# Revit family: P191568KX-114c_KSDG950E
name_source: partatom
category: Specialty Equipment
units: mm (PartAtom-declared; Revit-internal decimal feet)

## family parameters
Always vertical = Yes
Cut with Voids When Loaded = No
Enable Cutting in Views = No
Maintain Annotation Orientation = No
Part Type = Normal
Room Calculation Point = No
Round Connector Dimension = Use Diameter
Shared = No
Work Plane-Based = No

## types (1)
- KSDG950ESS
    Apparent Load = 40 VA
    Body Material = ARCAT - Metal - Steel - Stainless
    Clearance Material = ARCAT - Clearance
    Cooking Grate Material = ARCAT - Metal - Cast Iron 1/4" Plate
    Default Elevation = 0"
    Depth = 28 7/8"
    Description = 30-Inch 4-Burner Dual Fuel Downdraft Slide-In Range
Cuisinière bi-combustible à commandes frontales, 4 brûleurs, 30 po
    Dimension Guide = http://access.whirlpool.com Guide&sku=KSDG950ESS&language=EN
http://access.whirlpool.com Guide&sku=KSDG950ESS&language=FR
    Door Material = ARCAT - Metal - Steel - Stainless
    Family Name = COOKING
    Feature 1 = Downdraft
Évacuation descendante
    Feature 2 = Even-Heat™ True Convection
Convection véritable Even-Heat™
    Feature 3 = Steam Rack
Bac pour cuisson à vapeur
    Glass Material = ARCAT - Glass - Tempered - Black
    Handle Material = ARCAT - Metal - Steel - Gray
    Height = 36"
    Installation-Fabrication = http://access.whirlpool.com Instruction&sku=KSDG950ESS&language=EN
http://access.whirlpool.com Instruction&sku=KSDG950ESS&language=FR
    Knob Material = ARCAT - Metal - Steel - Gray
    Leg Material = ARCAT - Metal - Steel - Stainless
    Manufacturer = Kitchen Aid
    Model = KSDG950ESS
    Voltage = 0 V
    Width = 29 7/8"

## geometry (parser evidence)
native form markers: Sweep x5
no freeform markers — native parametric forms only
